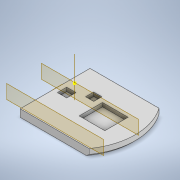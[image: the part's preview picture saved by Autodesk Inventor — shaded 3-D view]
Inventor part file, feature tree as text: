
AUTODESK INVENTOR PART (.ipt)
format: ipt  version: 2021 (Build 250183000, 183)  size: 450,560 bytes
history: native  units: in
note: dims shown in document units (in); Inventor stores cm internally (conversion verified against a paired STEP export)
features: sketch x11, extrude x9, fillet x4, plane x3, mirror x2, chamfer x1, other x1, pattern_circular x1
ambient origin geometry x8: Origin, YZ Plane, XZ Plane, XY Plane, X Axis, Y Axis, Z Axis, Center Point
bodies: Solid1 (feature_tree)
feature tree (32):
  extrude  "Extrusion1"  Depth=0.3701in TaperAngle=0.0deg
  chamfer  "Chamfer2"  Distance=0.2441in
  extrude  "Extrusion2"  Depth=0.1417in
  extrude  "Extrusion3"  Depth=0.2205in
  other  "Work Axis1"
  plane  "Work Plane1"
  extrude  "Extrusion4"  Depth=0.8268in
  fillet  "Fillet4"  Radius=0.3539in
  pattern_circular  "Circular Pattern2"  Angle=45.0deg  [1 undecoded]
  fillet  "Fillet7"  Radius=0.0394in
  extrude  "Initals"  Depth=0.3937in TaperAngle=240.0deg
  fillet  "Fillet9"  Radius=0.0315in
  fillet  "Fillet10"  Radius=1.1811in
  mirror  "Mirror6"
  sketch  "Sketch18"  dims[d15=0.0in d16=0.0in d17=0.2205in]
  plane  "Work Plane5"
  extrude  "Extrusion13"  Depth=0.3937in
  mirror  "Mirror7"
  extrude  "Extrusion15"  Depth=0.3937in
  extrude  "Extrusion16"  Depth=0.3937in
  plane  "Work Plane7"
  extrude  "Extrusion17"  Depth=0.3937in TaperAngle=0.0deg
  sketch  "Sketch1"  dims[d0=2.0472in d3=0.3701in d4=0.0in]
  sketch  "Sketch2"  dims[d5=1.4315in]
  sketch  "Sketch3"  dims[d6=0.7079in]
  sketch  "Sketch4"  dims[d7=0.3539in]
  sketch  "Sketch12"  dims[d8=0.4882in d9=0.2441in d10=0.0in]
  sketch  "Sketch13"  dims[d11=0.0in d14=0.1417in]
  sketch  "Sketch19"  dims[d18=0.2047in d19=0.0in d23=0.8268in d24=0.3539in]
  sketch  "Sketch22"  dims[d44=0.1417in]
  sketch  "Sketch23"  dims[d47=0.0in]
  sketch  "Sketch24"  dims[d48=0.0in d49=0.0in d51=0.0in d54=0.0394in d55=0.0in d56=45.0deg d58=0.0394in d59=0.1181in d60=1.9685in d61=240.0deg d72=0.0315in d80=1.1811in d81=0.5906in d82=0.9728in d83=0.4864in d84=0.0394in d85=0.0in d86=0.547in d87=0.2735in d88=0.0787in d89=0.0in d90=0.0787in d101=0.2362in d102=0.0315in d103=0.0315in d104=0.2953in d105=0.1575in d106=0.1969in d114=0.5906in d115=0.0in d116=0.0in d120=0.1575in d121=0.1575in d122=0.2362in d123=0.2362in d124=0.5354in d125=0.0787in d126=0.1378in d127=0.1378in d128=0.063in d129=0.0in d130=0.4331in d131=0.3937in d132=0.2362in d133=0.1969in d134=0.0in d135=0.0in d136=-0.0787in d137=0.0in d138=0.0in d91=0.0197in d92=0.0344in d93=0.0197in d94=0.0344in]
note: 1 required parameter value undecoded (feature->parameter linkage not recoverable at this tier; creation-order binding heuristic only, values carry confidence <= 0.55)
